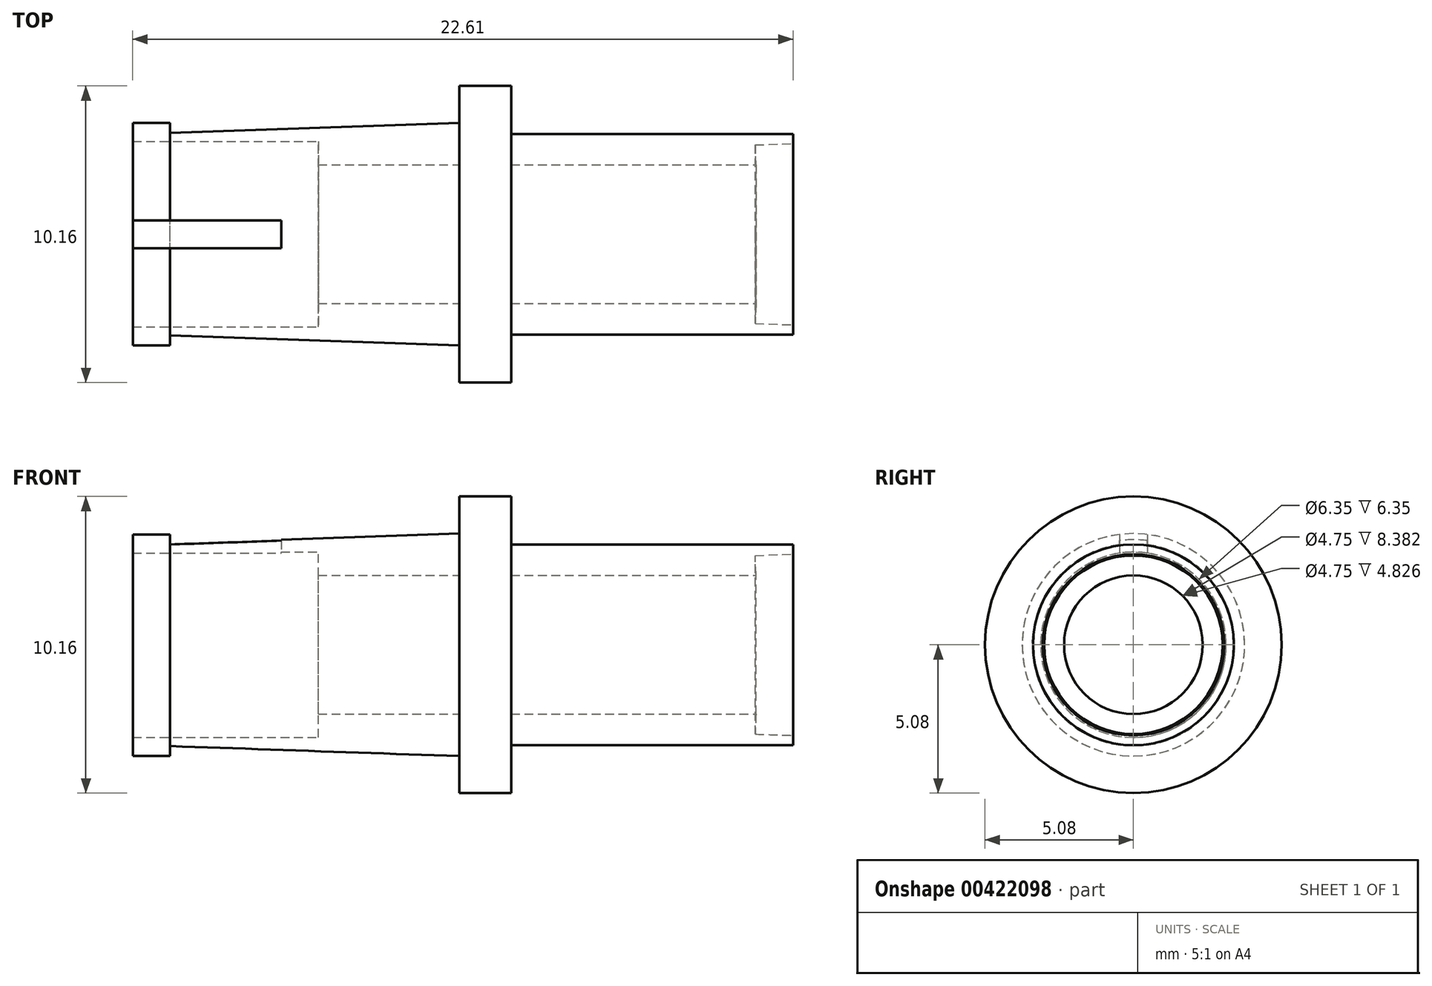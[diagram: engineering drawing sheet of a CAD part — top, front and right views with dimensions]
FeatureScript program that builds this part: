
annotation { "Feature Type Name" : "Feature", "Feature Type Description" : "" }
export const myFeature = defineFeature(function(context is Context, id is Id, definition is map)
    precondition{}
    {
        {
            var Q0;
            Q0=qCreatedBy(makeId("Front.planeOp"),FACE);
            var sketch = newSketch(context, id + "F0", { "sketchPlane" : qUnion([Q0])});
            skLineSegment(sketch, "E0", {"start": v(0, 0) * mm, "end": v(0, 2.37) * mm});
            skLineSegment(sketch, "E1", {"start": v(-11.18, 3.17) * mm, "end": v(-11.18, 3.8) * mm});
            skLineSegment(sketch, "E2", {"start": v(-11.18, 3.81) * mm, "end": v(-9.9, 3.81) * mm});
            skLineSegment(sketch, "E3", {"start": v(-9.9, 3.81) * mm, "end": v(-9.9, 3.47) * mm});
            skLineSegment(sketch, "E4", {"start": v(-9.9, 3.47) * mm, "end": v(0, 3.8) * mm});
            skLineSegment(sketch, "E5", {"start": v(0, 3.81) * mm, "end": v(0, 5.08) * mm});
            skLineSegment(sketch, "E6", {"start": v(0, 5.08) * mm, "end": v(1.78, 5.08) * mm});
            skLineSegment(sketch, "E7", {"start": v(1.78, 5.08) * mm, "end": v(1.78, 3.44) * mm});
            skLineSegment(sketch, "E8", {"start": v(1.78, 3.44) * mm, "end": v(11.43, 3.44) * mm});
            skLineSegment(sketch, "E9", {"start": v(10.16, 2.37) * mm, "end": v(1.78, 2.37) * mm});
            skLineSegment(sketch, "E10", {"start": v(1.78, 2.37) * mm, "end": v(1.78, 0) * mm});
            skLineSegment(sketch, "E11", {"start": v(1.78, 0) * mm, "end": v(0, 0) * mm});
            skLineSegment(sketch, "E12", {"start": v(0, 2.37) * mm, "end": v(-4.83, 2.37) * mm});
            skLineSegment(sketch, "E13", {"start": v(-4.83, 2.37) * mm, "end": v(-4.83, 3.18) * mm});
            skLineSegment(sketch, "E14", {"start": v(-4.83, 3.18) * mm, "end": v(-11.18, 3.17) * mm});
            skPoint(sketch, "E15.end.orphan", {"position": v(11.43, 3.81) * mm});
            skLineSegment(sketch, "E16", {"start": v(10.16, 2.37) * mm, "end": v(10.14, 3.06) * mm});
            skLineSegment(sketch, "E17", {"start": v(10.14, 3.06) * mm, "end": v(11.43, 3.1) * mm});
            skLineSegment(sketch, "E18", {"start": v(11.43, 3.1) * mm, "end": v(11.43, 3.44) * mm});
            skSolve(sketch);
        }
        {
            var Q0;
            Q0=makeQuery(id+"F0.imprint","IMPRINT",FACE,{"disambiguationData":[TD([[makeQuery(id+"F0.imprint","IMPRINT",EDGE,{"derivedFrom":sQuery(id+"F0.wireOp",EDGE,"E0")}),-1.0]])]});
            var Q1;
            Q1=sQuery(id+"F0.wireOp",EDGE,"E11");
            revolve(context, id + "F1", {"entities" : qUnion([Q0]), "axis" : qUnion([Q1]), "revolveType" : RevolveType.FULL});
        }
        {
            var Q0;
            Q0=makeQuery(id+"F1.opRevolve","SWEPT_FACE",FACE,{"disambiguationData":[OSD([sQuery(id+"F0.wireOp",EDGE,"E1")])]});
            var sketch = newSketch(context, id + "F2", { "sketchPlane" : qUnion([Q0])});
            skLineSegment(sketch, "E19.bottom", {"start": v(-0.47, 4.77) * mm, "end": v(0.47, 4.77) * mm});
            skLineSegment(sketch, "E19.top", {"start": v(-0.47, 1.58) * mm, "end": v(0.47, 1.58) * mm});
            skLineSegment(sketch, "E19.left", {"start": v(-0.47, 4.77) * mm, "end": v(-0.47, 1.58) * mm});
            skLineSegment(sketch, "E19.right", {"start": v(0.47, 4.77) * mm, "end": v(0.47, 1.58) * mm});
            skPoint(sketch, "E19.middle", {"position": v(0, 3.18) * mm});
            skSolve(sketch);
        }
        {
            var Q0;
            {var subQ0=sQuery(id+"F2.wireOp",EDGE,"E19.top");Q0=makeQuery(id+"F2.imprint","IMPRINT",FACE,{"disambiguationData":[TD([[makeQuery(id+"F2.imprint","IMPRINT",EDGE,{"derivedFrom":subQ0}),1.0]])]});}
            var Q1;
            {var subQ0=sQuery(id+"F2.wireOp",EDGE,"E19.bottom");Q1=makeQuery(id+"F2.imprint","IMPRINT",FACE,{"disambiguationData":[TD([[makeQuery(id+"F2.imprint","IMPRINT",EDGE,{"derivedFrom":subQ0}),-1.0]])]});}
            var Q2;
            {var subQ0=sQuery(id+"F2.wireOp",EDGE,"E19.left");var subQ1=sQuery(id+"F0.wireOp",EDGE,"E1");var subQ2=makeQuery(id+"F1.opRevolve","SWEPT_EDGE",EDGE,{"disambiguationData":[OSD([subQ1,sQuery(id+"F0.wireOp",EDGE,"E2")])]});var subQ3=makeQuery(id+"F2.imprint","INTERSECT",VERTEX,{"derivedFrom":[subQ2,subQ0]});Q2=makeQuery(id+"F2.imprint","IMPRINT",FACE,{"disambiguationData":[TD([[makeQuery(id+"F2.imprint","IMPRINT",EDGE,{"disambiguationData":[TD([[subQ3,-1.0]])],"derivedFrom":subQ0}),1.0]])]});}
            extrude(context, id + "F3", {"entities" : qUnion([Q0, Q1, Q2]), "operationType" : NewBodyOperationType.REMOVE, "oppositeDirection" : true, "depth" : 5.08 * mm});
        }
    });
